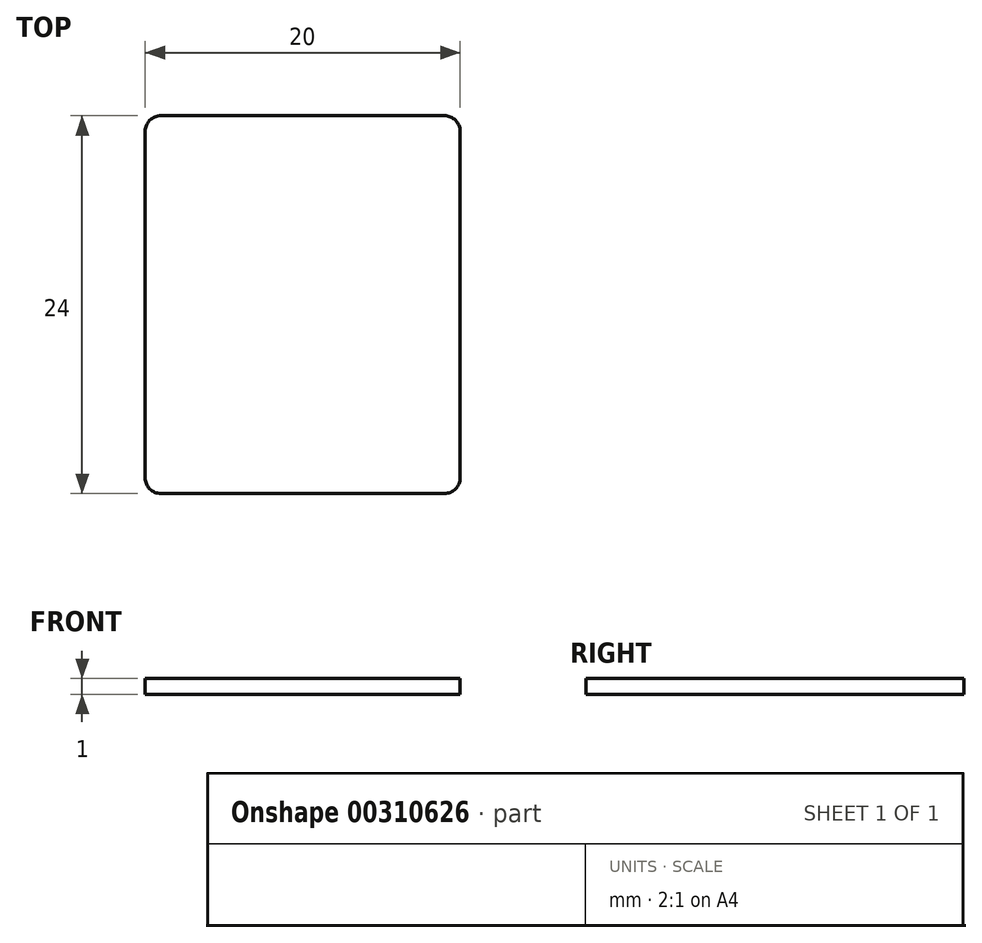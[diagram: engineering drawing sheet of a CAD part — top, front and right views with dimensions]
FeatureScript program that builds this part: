
annotation { "Feature Type Name" : "Feature", "Feature Type Description" : "" }
export const myFeature = defineFeature(function(context is Context, id is Id, definition is map)
    precondition{}
    {
        {
            var Q0;
            Q0=qCreatedBy(makeId("Front.planeOp"),FACE);
            var sketch = newSketch(context, id + "F0", { "sketchPlane" : qUnion([Q0])});
            skLineSegment(sketch, "E0.bottom", {"start": v(10, -0.5) * mm, "end": v(-10, -0.5) * mm});
            skLineSegment(sketch, "E0.top", {"start": v(10, 0.5) * mm, "end": v(-10, 0.5) * mm});
            skLineSegment(sketch, "E0.left", {"start": v(10, -0.5) * mm, "end": v(10, 0.5) * mm});
            skLineSegment(sketch, "E0.right", {"start": v(-10, -0.5) * mm, "end": v(-10, 0.5) * mm});
            skPoint(sketch, "E0.middle", {"position": v(0, 0) * mm});
            skSolve(sketch);
        }
        {
            var Q0;
            Q0=makeQuery(id+"F0.imprint","IMPRINT",FACE,{"disambiguationData":[TD([[makeQuery(id+"F0.imprint","IMPRINT",EDGE,{"derivedFrom":sQuery(id+"F0.wireOp",EDGE,"E0.bottom")}),-1.0]])]});
            extrude(context, id + "F1", {"entities" : qUnion([Q0]), "endBound" : BoundingType.SYMMETRIC, "depth" : 24 * mm});
        }
        {
            var Q0;
            Q0=makeQuery(id+"F1.opExtrude","CAP_EDGE",EDGE,{"disambiguationData":[OSD([sQuery(id+"F0.wireOp",EDGE,"E0.right")])],"isStart":false});
            var Q1;
            Q1=makeQuery(id+"F1.opExtrude","CAP_EDGE",EDGE,{"disambiguationData":[OSD([sQuery(id+"F0.wireOp",EDGE,"E0.left")])],"isStart":false});
            var Q2;
            Q2=makeQuery(id+"F1.opExtrude","CAP_EDGE",EDGE,{"disambiguationData":[OSD([sQuery(id+"F0.wireOp",EDGE,"E0.left")])],"isStart":true});
            var Q3;
            Q3=makeQuery(id+"F1.opExtrude","CAP_EDGE",EDGE,{"disambiguationData":[OSD([sQuery(id+"F0.wireOp",EDGE,"E0.right")])],"isStart":true});
            fillet(context, id + "F2", {"entities" : qUnion([Q0, Q1, Q2, Q3]), "radius" : 1 * mm, "tangentPropagation" : true, "allowEdgeOverflow" : false});
        }
    });
